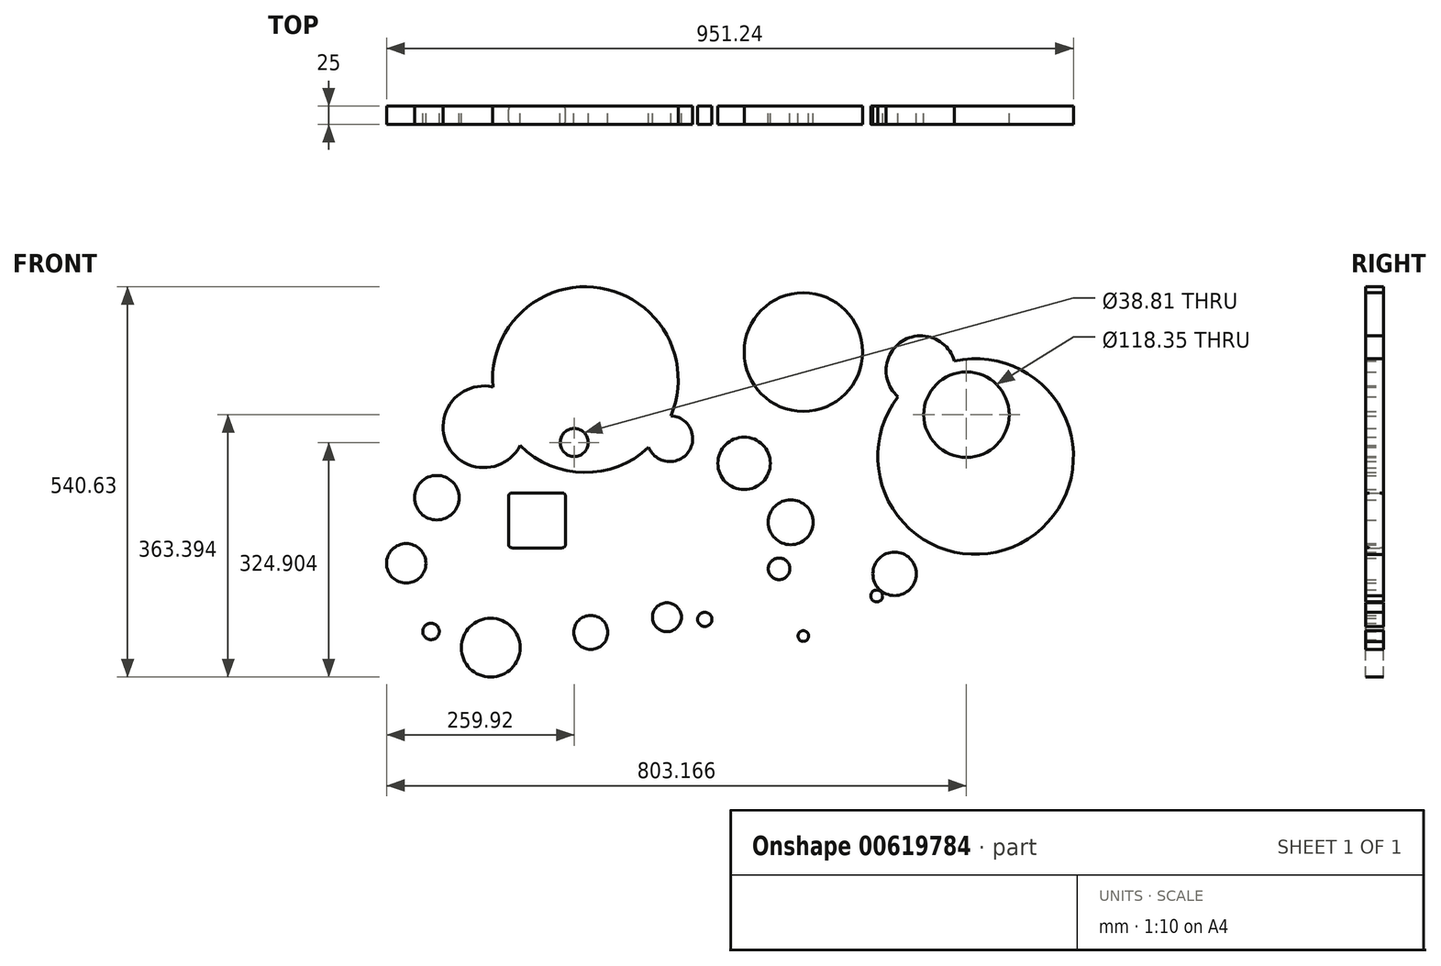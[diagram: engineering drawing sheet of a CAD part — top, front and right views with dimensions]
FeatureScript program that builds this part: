
annotation { "Feature Type Name" : "Feature", "Feature Type Description" : "" }
export const myFeature = defineFeature(function(context is Context, id is Id, definition is map)
    precondition{}
    {
        {
            var Q0;
            Q0=qCreatedBy(makeId("Front.planeOp"),FACE);
            var sketch = newSketch(context, id + "F0", { "sketchPlane" : qUnion([Q0])});
            skLineSegment(sketch, "E0.bottom", {"start": v(-81.63, 64.23) * mm, "end": v(-2.76, 64.23) * mm});
            skLineSegment(sketch, "E0.top", {"start": v(-81.63, -12) * mm, "end": v(-2.76, -12) * mm});
            skLineSegment(sketch, "E0.left", {"start": v(-81.63, 64.23) * mm, "end": v(-81.63, -12) * mm});
            skLineSegment(sketch, "E0.right", {"start": v(-2.76, 64.23) * mm, "end": v(-2.76, -12) * mm});
            skSolve(sketch);
        }
        {
            var Q0;
            Q0 = qSketchRegion(id + "F0", true);
            extrude(context, id + "F1", {"entities" : qUnion([Q0]), "depth" : 25 * mm, "offsetDistance" : 25 * mm});
        }
        {
            var Q0;
            Q0=makeQuery(id+"F1.opExtrude","SWEPT_EDGE",EDGE,{"disambiguationData":[OSD([sQuery(id+"F0.wireOp",EDGE,"E0.top"),sQuery(id+"F0.wireOp",EDGE,"E0.right")])]});
            var Q1;
            Q1=makeQuery(id+"F1.opExtrude","SWEPT_EDGE",EDGE,{"disambiguationData":[OSD([sQuery(id+"F0.wireOp",EDGE,"E0.bottom"),sQuery(id+"F0.wireOp",EDGE,"E0.right")])]});
            var Q2;
            Q2=makeQuery(id+"F1.opExtrude","SWEPT_EDGE",EDGE,{"disambiguationData":[OSD([sQuery(id+"F0.wireOp",EDGE,"E0.bottom"),sQuery(id+"F0.wireOp",EDGE,"E0.left")])]});
            var Q3;
            Q3=makeQuery(id+"F1.opExtrude","CAP_EDGE",EDGE,{"disambiguationData":[OSD([sQuery(id+"F0.wireOp",EDGE,"E0.bottom")])],"isStart":true});
            var Q4;
            Q4=makeQuery(id+"F1.opExtrude","CAP_EDGE",EDGE,{"disambiguationData":[OSD([sQuery(id+"F0.wireOp",EDGE,"E0.bottom")])],"isStart":false});
            var Q5;
            Q5=makeQuery(id+"F1.opExtrude","CAP_EDGE",EDGE,{"disambiguationData":[OSD([sQuery(id+"F0.wireOp",EDGE,"E0.top")])],"isStart":false});
            var Q6;
            Q6=makeQuery(id+"F1.opExtrude","SWEPT_EDGE",EDGE,{"disambiguationData":[OSD([sQuery(id+"F0.wireOp",EDGE,"E0.top"),sQuery(id+"F0.wireOp",EDGE,"E0.left")])]});
            var Q7;
            Q7=makeQuery(id+"F1.opExtrude","CAP_EDGE",EDGE,{"disambiguationData":[OSD([sQuery(id+"F0.wireOp",EDGE,"E0.top")])],"isStart":true});
            var Q8;
            Q8=makeQuery(id+"F1.opExtrude","CAP_EDGE",EDGE,{"disambiguationData":[OSD([sQuery(id+"F0.wireOp",EDGE,"E0.left")])],"isStart":true});
            var Q9;
            Q9=makeQuery(id+"F1.opExtrude","CAP_EDGE",EDGE,{"disambiguationData":[OSD([sQuery(id+"F0.wireOp",EDGE,"E0.left")])],"isStart":false});
            var Q10;
            Q10=makeQuery(id+"F1.opExtrude","CAP_EDGE",EDGE,{"disambiguationData":[OSD([sQuery(id+"F0.wireOp",EDGE,"E0.right")])],"isStart":true});
            var Q11;
            Q11=makeQuery(id+"F1.opExtrude","CAP_EDGE",EDGE,{"disambiguationData":[OSD([sQuery(id+"F0.wireOp",EDGE,"E0.right")])],"isStart":false});
            fillet(context, id + "F2", {"entities" : qUnion([Q0, Q1, Q2, Q3, Q4, Q5, Q6, Q7, Q8, Q9, Q10, Q11]), "radius" : 5 * mm, "tangentPropagation" : true, "allowEdgeOverflow" : false});
        }
        {
            var Q0;
            Q0=qCreatedBy(makeId("Front.planeOp"),FACE);
            var sketch = newSketch(context, id + "F3", { "sketchPlane" : qUnion([Q0])});
            skCircle(sketch, "E1", {"center": v(9.34, 133.96) * mm, "radius": 19.4 * mm});
            skCircle(sketch, "E2", {"center": v(141.8, 139.25) * mm, "radius": 31.66 * mm});
            skCircle(sketch, "E3", {"center": v(244.66, 105.08) * mm, "radius": 36.32 * mm});
            skCircle(sketch, "E4", {"center": v(309.2, 23.53) * mm, "radius": 31.08 * mm});
            skCircle(sketch, "E5", {"center": v(293.07, -40.96) * mm, "radius": 15 * mm});
            skCircle(sketch, "E6", {"center": v(190.2, -111) * mm, "radius": 9.9 * mm});
            skCircle(sketch, "E7", {"center": v(137.76, -107.98) * mm, "radius": 20 * mm});
            skCircle(sketch, "E8", {"center": v(32.2, -129.04) * mm, "radius": 23.53 * mm});
            skCircle(sketch, "E9", {"center": v(-106.3, -150.2) * mm, "radius": 40.74 * mm});
            skCircle(sketch, "E10", {"center": v(-189, -127.68) * mm, "radius": 11.43 * mm});
            skCircle(sketch, "E11", {"center": v(-223.29, -33.37) * mm, "radius": 27.29 * mm});
            skCircle(sketch, "E12", {"center": v(-180.93, 57.52) * mm, "radius": 30.84 * mm});
            skCircle(sketch, "E13", {"center": v(-115.71, 155.68) * mm, "radius": 56.53 * mm});
            skCircle(sketch, "E14", {"center": v(24.8, 221.12) * mm, "radius": 128.56 * mm});
            skCircle(sketch, "E15", {"center": v(326.68, 259.19) * mm, "radius": 82.04 * mm});
            skCircle(sketch, "E16", {"center": v(489.39, 233.55) * mm, "radius": 48.1 * mm});
            skCircle(sketch, "E17", {"center": v(552.59, 172.45) * mm, "radius": 59.18 * mm});
            skCircle(sketch, "E18", {"center": v(565.17, 114.63) * mm, "radius": 135.5 * mm});
            skCircle(sketch, "E19", {"center": v(453.08, -47.89) * mm, "radius": 30.13 * mm});
            skCircle(sketch, "E20", {"center": v(428.2, -78.6) * mm, "radius": 8.24 * mm});
            skCircle(sketch, "E21", {"center": v(326.68, -134.13) * mm, "radius": 7.4 * mm});
            skSolve(sketch);
        }
        {
            var Q0;
            Q0 = qSketchRegion(id + "F3", true);
            extrude(context, id + "F4", {"entities" : qUnion([Q0]), "depth" : 25 * mm, "offsetDistance" : 25 * mm});
        }
    });
